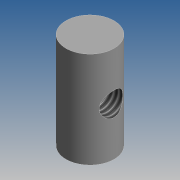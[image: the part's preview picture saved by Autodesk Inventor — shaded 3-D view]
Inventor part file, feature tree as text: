
AUTODESK INVENTOR PART (.ipt)
format: ipt  version: 2015 SP1 (Build 190203100, 203)  size: 198,656 bytes
history: native  units: mm
features: sketch x2, extrude x1, plane x1, hole x1
ambient origin geometry x8: Origin, YZ Plane, XZ Plane, XY Plane, X Axis, Y Axis, Z Axis, Center Point
bodies: Solid1 (feature_tree)
feature tree (5):
  extrude  "Extrusion1"  Depth=10.0mm TaperAngle=0.0deg
  plane  "Work Plane1"
  hole  "Hole1"  [1 undecoded]
  sketch  "Sketch1"  dims[d0=5.0mm d1=10.0mm d2=0.0mm]
  sketch  "Sketch3"  dims[d3=3.0mm d4=2.459mm d5=6.0mm d6=4.0mm d7=2.0mm d8=90.0deg d9=8.8mm d10=20.594885mm]
note: 1 required parameter value undecoded (feature->parameter linkage not recoverable at this tier; creation-order binding heuristic only, values carry confidence <= 0.55)
